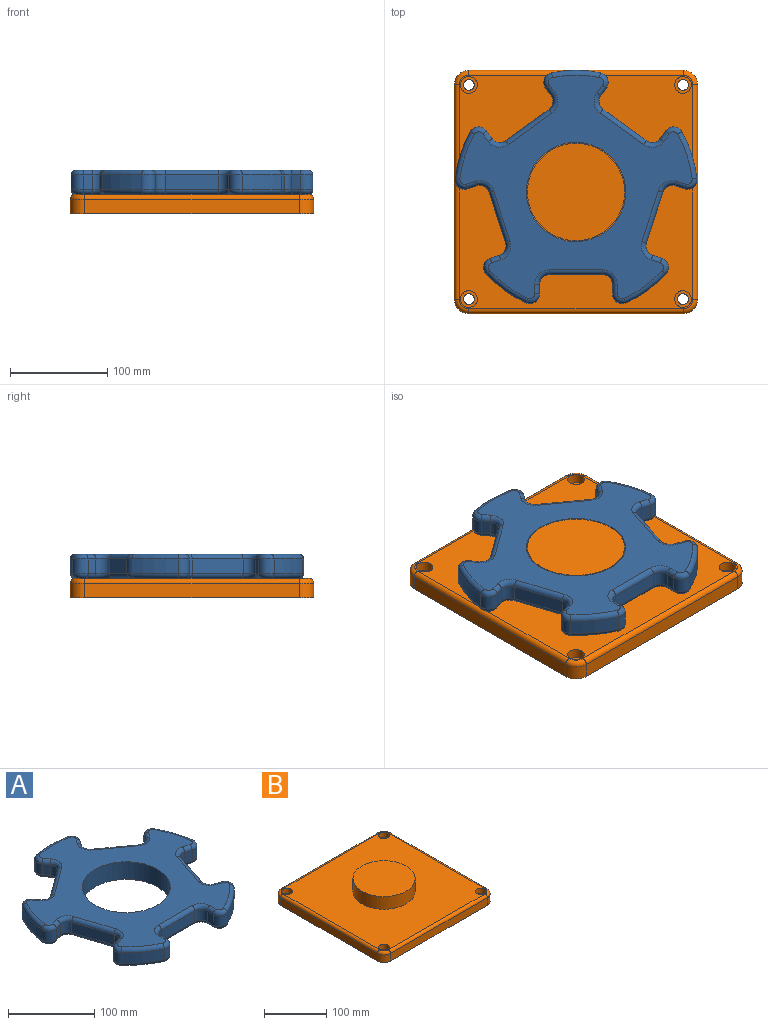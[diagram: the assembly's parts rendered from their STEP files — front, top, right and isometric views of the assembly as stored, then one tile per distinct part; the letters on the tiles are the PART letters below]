
ASSEMBLY  parts=2 mates=1
PART A: 123 faces, bbox 268.9x258.5x25 mm
  f0: plane 238.57x229.73mm, normal (0,0,1), area 21505.7mm2, adj f6,f43,f44,f45,f46,f47,f48,f49
  f1: plane 238.57x229.73mm, normal (0,0,-1), area 21505.7mm2, adj f6,f83,f84,f85,f86,f87,f88,f89
  f2: cylinder r=125mm len=40.68mm, axis (0,0,-1), area 759.5mm2, adj f13,f42,f51,f91
  f3: cylinder r=125mm len=47.82mm, axis (0,0,-1), area 759.5mm2, adj f35,f41,f67,f107
  f4: cylinder r=125mm len=50.29mm, axis (0,0,-1), area 759.5mm2, adj f28,f34,f82,f122
  f5: cylinder r=125mm len=47.82mm, axis (0,0,-1), area 759.5mm2, adj f21,f27,f66,f106
  f6: cylinder r=51mm len=102mm, axis (0,0,-1), area 8011.1mm2, adj f0,f1
  f7: cylinder r=125mm len=40.68mm, axis (0,0,-1), area 759.5mm2, adj f14,f20,f50,f90
  f8: plane 15x9.73mm, normal (-1,0,0), area 146mm2, adj f11,f14,f46,f86
  f9: plane 55x15mm, normal (0,-1,0), area 825mm2, adj f11,f12,f43,f83
  f10: plane 15x9.73mm, normal (1,0,0), area 146mm2, adj f12,f13,f47,f87
  f11: cylinder r=10mm len=15mm, axis (0,0,-1), area 235.6mm2, adj f8,f9,f44,f84
  f12: cylinder r=10mm len=15mm, axis (0,0,-1), area 235.6mm2, adj f9,f10,f45,f85
  f13: cylinder r=10mm len=15mm, axis (0,0,-1), area 299.5mm2, adj f2,f10,f49,f89
  f14: cylinder r=10mm len=15mm, axis (0,0,-1), area 299.5mm2, adj f7,f8,f48,f88
  f15: plane 15x9.26mm, normal (-0.31,-0.95,0), area 146mm2, adj f18,f21,f62,f102
  f16: plane 52.31x17mm, normal (0.95,-0.31,0), area 825mm2, adj f18,f19,f58,f98
  f17: plane 15x9.26mm, normal (0.31,0.95,0), area 146mm2, adj f19,f20,f54,f94
  f18: cylinder r=10mm len=15mm, axis (0,0,-1), area 235.6mm2, adj f15,f16,f60,f100
  f19: cylinder r=10mm len=15mm, axis (0,0,-1), area 235.6mm2, adj f16,f17,f56,f96
  f20: cylinder r=10mm len=16.25mm, axis (0,0,-1), area 299.5mm2, adj f7,f17,f52,f92
  f21: cylinder r=10mm len=15mm, axis (0,0,-1), area 299.5mm2, adj f5,f15,f64,f104
  f22: plane 15x7.87mm, normal (0.81,-0.59,0), area 146mm2, adj f25,f28,f78,f118
  f23: plane 44.5x32.33mm, normal (0.59,0.81,0), area 825mm2, adj f25,f26,f74,f114
  f24: plane 15x7.87mm, normal (-0.81,0.59,0), area 146mm2, adj f26,f27,f70,f110
  f25: cylinder r=10mm len=15mm, axis (0,0,-1), area 235.6mm2, adj f22,f23,f76,f116
  f26: cylinder r=10mm len=15mm, axis (0,0,-1), area 235.6mm2, adj f23,f24,f72,f112
  f27: cylinder r=10mm len=16.78mm, axis (0,0,-1), area 299.5mm2, adj f5,f24,f68,f108
  f28: cylinder r=10mm len=15.67mm, axis (0,0,-1), area 299.5mm2, adj f4,f22,f80,f120
  f29: plane 15x7.87mm, normal (0.81,0.59,0), area 146mm2, adj f32,f35,f71,f111
  f30: plane 44.5x32.33mm, normal (-0.59,0.81,0), area 825mm2, adj f32,f33,f75,f115
  f31: plane 15x7.87mm, normal (-0.81,-0.59,0), area 146mm2, adj f33,f34,f79,f119
  f32: cylinder r=10mm len=15mm, axis (0,0,-1), area 235.6mm2, adj f29,f30,f73,f113
  f33: cylinder r=10mm len=15mm, axis (0,0,-1), area 235.6mm2, adj f30,f31,f77,f117
  f34: cylinder r=10mm len=15.67mm, axis (0,0,-1), area 299.5mm2, adj f4,f31,f81,f121
  f35: cylinder r=10mm len=16.78mm, axis (0,0,-1), area 299.5mm2, adj f3,f29,f69,f109
  f36: plane 15x9.26mm, normal (-0.31,0.95,0), area 146mm2, adj f39,f42,f55,f95
  f37: plane 52.31x17mm, normal (-0.95,-0.31,0), area 825mm2, adj f39,f40,f59,f99
  f38: plane 15x9.26mm, normal (0.31,-0.95,0), area 146mm2, adj f40,f41,f63,f103
  f39: cylinder r=10mm len=15mm, axis (0,0,-1), area 235.6mm2, adj f36,f37,f57,f97
  f40: cylinder r=10mm len=15mm, axis (0,0,-1), area 235.6mm2, adj f37,f38,f61,f101
  f41: cylinder r=10mm len=15mm, axis (0,0,-1), area 299.5mm2, adj f3,f38,f65,f105
  f42: cylinder r=10mm len=16.25mm, axis (0,0,-1), area 299.5mm2, adj f2,f36,f53,f93
  f43: cylinder r=5mm len=55mm, axis (1,0,0), area 432mm2, adj f0,f9,f44,f45
  f44: torus R=15mm, axis (0,0,1), area 145.8mm2, adj f0,f11,f43,f46
  f45: torus R=15mm, axis (0,0,1), area 145.8mm2, adj f0,f12,f43,f47
  f46: cylinder r=5mm len=9.73mm, axis (0,-1,0), area 76.4mm2, adj f0,f8,f44,f48
  f47: cylinder r=5mm len=9.73mm, axis (0,1,0), area 76.4mm2, adj f0,f10,f45,f49
  f48: torus R=5mm, axis (0,0,1), area 128.3mm2, adj f0,f14,f46,f50
  f49: torus R=5mm, axis (0,0,1), area 128.3mm2, adj f0,f13,f47,f51
  f50: torus R=120mm, axis (0,0,1), area 391.9mm2, adj f0,f7,f48,f52
  f51: torus R=120mm, axis (0,0,1), area 391.9mm2, adj f0,f2,f49,f53
  f52: torus R=5mm, axis (0,0,1), area 128.3mm2, adj f0,f20,f50,f54
  f53: torus R=5mm, axis (0,0,1), area 128.3mm2, adj f0,f42,f51,f55
  f54: cylinder r=5mm len=10.8mm, axis (-0.95,0.31,0), area 76.4mm2, adj f0,f17,f52,f56
  f55: cylinder r=5mm len=10.8mm, axis (-0.95,-0.31,0), area 76.4mm2, adj f0,f36,f53,f57
  f56: torus R=15mm, axis (0,0,1), area 145.8mm2, adj f0,f19,f54,f58
  f57: torus R=15mm, axis (0,0,1), area 145.8mm2, adj f0,f39,f55,f59
  f58: cylinder r=5mm len=53.85mm, axis (0.31,0.95,0), area 432mm2, adj f0,f16,f56,f60
  f59: cylinder r=5mm len=53.85mm, axis (0.31,-0.95,0), area 432mm2, adj f0,f37,f57,f61
  f60: torus R=15mm, axis (0,0,1), area 145.8mm2, adj f0,f18,f58,f62
  f61: torus R=15mm, axis (0,0,1), area 145.8mm2, adj f0,f40,f59,f63
  f62: cylinder r=5mm len=10.8mm, axis (0.95,-0.31,0), area 76.4mm2, adj f0,f15,f60,f64
  f63: cylinder r=5mm len=10.8mm, axis (0.95,0.31,0), area 76.4mm2, adj f0,f38,f61,f65
  f64: torus R=5mm, axis (0,0,1), area 128.3mm2, adj f0,f21,f62,f66
  f65: torus R=5mm, axis (0,0,1), area 128.3mm2, adj f0,f41,f63,f67
  f66: torus R=120mm, axis (0,0,1), area 391.9mm2, adj f0,f5,f64,f68
  f67: torus R=120mm, axis (0,0,1), area 391.9mm2, adj f0,f3,f65,f69
  f68: torus R=5mm, axis (0,0,1), area 128.3mm2, adj f0,f27,f66,f70
  f69: torus R=5mm, axis (0,0,1), area 128.3mm2, adj f0,f35,f67,f71
  f70: cylinder r=5mm len=10.81mm, axis (-0.59,-0.81,0), area 76.4mm2, adj f0,f24,f68,f72
  f71: cylinder r=5mm len=10.81mm, axis (-0.59,0.81,0), area 76.4mm2, adj f0,f29,f69,f73
  f72: torus R=15mm, axis (0,0,1), area 145.8mm2, adj f0,f26,f70,f74
  f73: torus R=15mm, axis (0,0,1), area 145.8mm2, adj f0,f32,f71,f75
  f74: cylinder r=5mm len=47.44mm, axis (-0.81,0.59,0), area 432mm2, adj f0,f23,f72,f76
  f75: cylinder r=5mm len=47.44mm, axis (-0.81,-0.59,0), area 432mm2, adj f0,f30,f73,f77
  f76: torus R=15mm, axis (0,0,1), area 145.8mm2, adj f0,f25,f74,f78
  f77: torus R=15mm, axis (0,0,1), area 145.8mm2, adj f0,f33,f75,f79
  f78: cylinder r=5mm len=10.81mm, axis (0.59,0.81,0), area 76.4mm2, adj f0,f22,f76,f80
  f79: cylinder r=5mm len=10.81mm, axis (0.59,-0.81,0), area 76.4mm2, adj f0,f31,f77,f81
  f80: torus R=5mm, axis (0,0,1), area 128.3mm2, adj f0,f28,f78,f82
  f81: torus R=5mm, axis (0,0,1), area 128.3mm2, adj f0,f34,f79,f82
  f82: torus R=120mm, axis (0,0,1), area 391.9mm2, adj f0,f4,f80,f81
  f83: cylinder r=5mm len=55mm, axis (-1,0,0), area 432mm2, adj f1,f9,f84,f85
  f84: torus R=15mm, axis (0,0,1), area 145.8mm2, adj f1,f11,f83,f86
  f85: torus R=15mm, axis (0,0,1), area 145.8mm2, adj f1,f12,f83,f87
  f86: cylinder r=5mm len=9.73mm, axis (0,1,0), area 76.4mm2, adj f1,f8,f84,f88
  f87: cylinder r=5mm len=9.73mm, axis (0,-1,0), area 76.4mm2, adj f1,f10,f85,f89
  f88: torus R=5mm, axis (0,0,1), area 128.3mm2, adj f1,f14,f86,f90
  f89: torus R=5mm, axis (0,0,1), area 128.3mm2, adj f1,f13,f87,f91
  f90: torus R=120mm, axis (0,0,1), area 391.9mm2, adj f1,f7,f88,f92
  f91: torus R=120mm, axis (0,0,1), area 391.9mm2, adj f1,f2,f89,f93
  f92: torus R=5mm, axis (0,0,1), area 128.3mm2, adj f1,f20,f90,f94
  f93: torus R=5mm, axis (0,0,1), area 128.3mm2, adj f1,f42,f91,f95
  f94: cylinder r=5mm len=10.8mm, axis (0.95,-0.31,0), area 76.4mm2, adj f1,f17,f92,f96
  f95: cylinder r=5mm len=10.8mm, axis (0.95,0.31,0), area 76.4mm2, adj f1,f36,f93,f97
  f96: torus R=15mm, axis (0,0,1), area 145.8mm2, adj f1,f19,f94,f98
  f97: torus R=15mm, axis (0,0,1), area 145.8mm2, adj f1,f39,f95,f99
  f98: cylinder r=5mm len=53.85mm, axis (-0.31,-0.95,0), area 432mm2, adj f1,f16,f96,f100
  f99: cylinder r=5mm len=53.85mm, axis (-0.31,0.95,0), area 432mm2, adj f1,f37,f97,f101
  f100: torus R=15mm, axis (0,0,1), area 145.8mm2, adj f1,f18,f98,f102
  f101: torus R=15mm, axis (0,0,1), area 145.8mm2, adj f1,f40,f99,f103
  f102: cylinder r=5mm len=10.8mm, axis (-0.95,0.31,0), area 76.4mm2, adj f1,f15,f100,f104
  f103: cylinder r=5mm len=10.8mm, axis (-0.95,-0.31,0), area 76.4mm2, adj f1,f38,f101,f105
  f104: torus R=5mm, axis (0,0,1), area 128.3mm2, adj f1,f21,f102,f106
  f105: torus R=5mm, axis (0,0,1), area 128.3mm2, adj f1,f41,f103,f107
  f106: torus R=120mm, axis (0,0,1), area 391.9mm2, adj f1,f5,f104,f108
  f107: torus R=120mm, axis (0,0,1), area 391.9mm2, adj f1,f3,f105,f109
  f108: torus R=5mm, axis (0,0,1), area 128.3mm2, adj f1,f27,f106,f110
  f109: torus R=5mm, axis (0,0,1), area 128.3mm2, adj f1,f35,f107,f111
  f110: cylinder r=5mm len=10.81mm, axis (0.59,0.81,0), area 76.4mm2, adj f1,f24,f108,f112
  f111: cylinder r=5mm len=10.81mm, axis (0.59,-0.81,0), area 76.4mm2, adj f1,f29,f109,f113
  f112: torus R=15mm, axis (0,0,1), area 145.8mm2, adj f1,f26,f110,f114
  f113: torus R=15mm, axis (0,0,1), area 145.8mm2, adj f1,f32,f111,f115
  f114: cylinder r=5mm len=47.44mm, axis (0.81,-0.59,0), area 432mm2, adj f1,f23,f112,f116
  f115: cylinder r=5mm len=47.44mm, axis (0.81,0.59,0), area 432mm2, adj f1,f30,f113,f117
  f116: torus R=15mm, axis (0,0,1), area 145.8mm2, adj f1,f25,f114,f118
  f117: torus R=15mm, axis (0,0,1), area 145.8mm2, adj f1,f33,f115,f119
  f118: cylinder r=5mm len=10.81mm, axis (-0.59,-0.81,0), area 76.4mm2, adj f1,f22,f116,f120
  f119: cylinder r=5mm len=10.81mm, axis (-0.59,0.81,0), area 76.4mm2, adj f1,f31,f117,f121
  f120: torus R=5mm, axis (0,0,1), area 128.3mm2, adj f1,f28,f118,f122
  f121: torus R=5mm, axis (0,0,1), area 128.3mm2, adj f1,f34,f119,f122
  f122: torus R=120mm, axis (0,0,1), area 391.9mm2, adj f1,f4,f120,f121
PART B: 32 faces, bbox 252.5x252.5x45 mm
  f0: plane 220x15mm, normal (1,0,0), area 3300mm2, adj f5,f8,f11,f27
  f1: plane 220x15mm, normal (0,1,0), area 3300mm2, adj f5,f8,f9,f31
  f2: plane 220x15mm, normal (-1,0,0), area 3300mm2, adj f5,f9,f10,f28
  f3: plane 220x15mm, normal (0,-1,0), area 3300mm2, adj f5,f10,f11,f24
  f4: plane 240x240mm, normal (0,0,1), area 48725.4mm2, adj f6,f14,f17,f20,f23,f24,f25,f26
  f5: plane 250x250mm, normal (0,0,-1), area 61926.7mm2, adj f0,f1,f2,f3,f8,f9,f10,f11
  f6: cylinder r=50mm len=100mm, axis (0,0,-1), area 7854mm2, adj f4,f7
  f7: plane 100x100mm, normal (0,0,1), area 7854mm2, adj f6
  f8: cylinder r=15mm len=15mm, axis (0,0,-1), area 353.4mm2, adj f0,f1,f5,f29
  f9: cylinder r=15mm len=15mm, axis (0,0,1), area 353.4mm2, adj f1,f2,f5,f30
  f10: cylinder r=15mm len=15mm, axis (0,0,-1), area 353.4mm2, adj f2,f3,f5,f26
  f11: cylinder r=15mm len=15mm, axis (0,0,1), area 353.4mm2, adj f0,f3,f5,f25
  f12: cylinder r=5.5mm len=11mm, axis (0,0,1), area 345.6mm2, adj f5,f13
  f13: plane 17.25x17.25mm, normal (0,0,1), area 138.7mm2, adj f12,f14
  f14: cylinder r=8.62mm len=17.25mm, axis (0,0,1), area 541.9mm2, adj f4,f13
  f15: cylinder r=5.5mm len=11mm, axis (0,0,1), area 345.6mm2, adj f5,f16
  f16: plane 17.25x17.25mm, normal (0,0,1), area 138.7mm2, adj f15,f17
  f17: cylinder r=8.62mm len=17.25mm, axis (0,0,1), area 541.9mm2, adj f4,f16
  f18: cylinder r=5.5mm len=11mm, axis (0,0,1), area 345.6mm2, adj f5,f19
  f19: plane 17.25x17.25mm, normal (0,0,1), area 138.7mm2, adj f18,f20
  f20: cylinder r=8.62mm len=17.25mm, axis (0,0,1), area 541.9mm2, adj f4,f19
  f21: cylinder r=5.5mm len=11mm, axis (0,0,1), area 345.6mm2, adj f5,f22
  f22: plane 17.25x17.25mm, normal (0,0,1), area 138.7mm2, adj f21,f23
  f23: cylinder r=8.62mm len=17.25mm, axis (0,0,1), area 541.9mm2, adj f4,f22
  f24: cylinder r=5mm len=220mm, axis (-1,0,0), area 1727.9mm2, adj f3,f4,f25,f26
  f25: torus R=10mm, axis (0,0,1), area 162.6mm2, adj f4,f11,f24,f27
  f26: torus R=10mm, axis (0,0,1), area 162.6mm2, adj f4,f10,f24,f28
  f27: cylinder r=5mm len=220mm, axis (0,-1,0), area 1727.9mm2, adj f0,f4,f25,f29
  f28: cylinder r=5mm len=220mm, axis (0,1,0), area 1727.9mm2, adj f2,f4,f26,f30
  f29: torus R=10mm, axis (0,0,1), area 162.6mm2, adj f4,f8,f27,f31
  f30: torus R=10mm, axis (0,0,1), area 162.6mm2, adj f4,f9,f28,f31
  f31: cylinder r=5mm len=220mm, axis (1,0,0), area 1727.9mm2, adj f1,f4,f29,f30
PLACE A at identity
PLACE B at identity
MATE revolute A.f2 <-> B.f6  axis (0,0,1) through (0,0,45)mm
